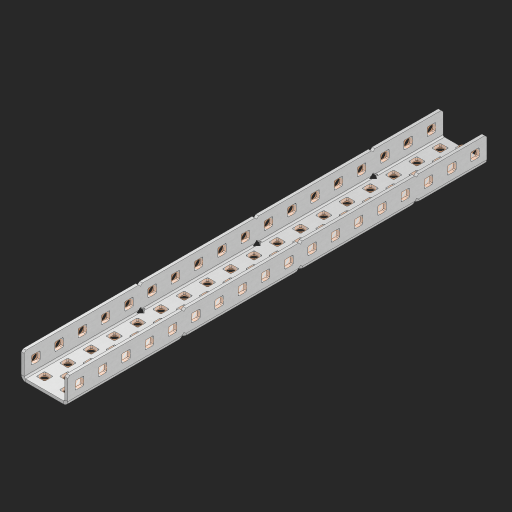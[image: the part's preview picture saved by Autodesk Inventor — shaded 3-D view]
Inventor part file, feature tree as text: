
AUTODESK INVENTOR PART (.ipt)
format: ipt  version: 2023 (Build 270158000, 158)  size: 1,305,088 bytes
history: native  units: in
note: dims shown in document units (in); Inventor stores cm internally (conversion verified against a paired STEP export)
features: other x97, extrude x88, sheet_metal_op x11, sketch x10, pattern_linear x2, mirror x1, chamfer x1
ambient origin geometry x8: Origin, YZ Plane, XZ Plane, XY Plane, X Axis, Y Axis, Z Axis, Center Point
bodies: Solid1 (feature_tree), Body (feature_tree)
feature tree (210):
  sheet_metal_op  "Flanges"
  other  "Flange Pattern Plane"
  other  "Flange Pattern Sketch"
  sheet_metal_op  "Flange Pattern"
  sheet_metal_op  "Body Pattern"
  pattern_linear  "Center Pattern"  Spacing1=0.0625in  [1 undecoded]
  other  "Arc Length"
  mirror  "Notch Mirror"
  pattern_linear  "Notch Pattern"  Spacing1=0.182in  [1 undecoded]
  chamfer  "End Chamfer"
  extrude  "Half Cut"  Depth=0.02in
  sketch  "Sketch1"  dims[d0=1.0in]
  other  "Plate1"
  sketch  "Sketch2"  dims[d1=9.0in]
  other  "Plate2"
  sheet_metal_op  "Bend1"
  sheet_metal_op  "Corner1"
  sketch  "Sketch3"  dims[d2=0.0625in]
  sketch  "Sketch7"  dims[d3=0.0625in]
  other  "Srf1"
  other  "Srf2"
  sketch  "Sketch8"  dims[d4=0.0312in]
  sketch  "Sketch9"  dims[d5=0.125in]
  other  "Srf91"
  sheet_metal_op  "Body Pattern Sketch"
  other  "Srf92"
  sketch  "Sketch13"  dims[d6=0.0625in]
  sketch  "Sketch14"  dims[d7=0.5in d8=90.0deg d9=0.0312in]
  sketch  "Sketch15"  dims[d10=0.25in]
  sketch  "Sketch16"  dims[d11=0.0625in d12=0.0625in d16=0.182in d17=0.02in d18=0.0625in d19=0.0in d20=0.25in d21=0.25in d38=7.0866in d40=0.5in d41=0.7874in d43=1.0in d46=0.172in d47=1.0in d48=0.0in d49=0.182in d50=0.02in d51=0.25in d52=0.25in d53=0.0625in d54=0.0in d55=0.172in d56=1.0in d57=0.0in d58=0.25in d60=7.0866in d62=0.5in d63=0.7874in d65=0.5in d85=0.1473in d86=0.1782in d88=0.04in d89=0.0625in d90=0.0in d91=0.04in d92=0.0491in d95=2.5in d96=0.04in d97=0.25in d98=45.0deg d99=0.25in d100=0.5in d101=0.0in d102=2.497in d106=0.182in d107=0.02in d108=0.5in d109=0.5in d110=0.0625in d111=0.0in d112=0.172in d113=0.5in d114=0.0in d117=0.5in d118=0.5in d119=0.5in]
  other  "Srf786"
  other  "Srf823"
  other  "Srf824"
  other  "Srf825"
  other  "Srf826"
  other  "Srf827"
  other  "Srf828"
  other  "Srf829"
  other  "Srf856"
  other  "Srf857"
  other  "Srf858"
  other  "Srf859"
  other  "Srf860"
  other  "Srf861"
  other  "Srf862"
  other  "Srf889"
  other  "Srf890"
  other  "Srf891"
  other  "Srf892"
  other  "Srf893"
  other  "Srf894"
  other  "Srf895"
  other  "Srf896"
  other  "Srf922"
  other  "Srf923"
  other  "Srf924"
  other  "Srf925"
  other  "Srf926"
  other  "Srf959"
  other  "Srf960"
  other  "Srf961"
  other  "Srf962"
  other  "Srf963"
  other  "Srf996"
  other  "Srf997"
  other  "Srf998"
  other  "Srf999"
  other  "Srf1000"
  other  "Srf1143"
  other  "Srf1144"
  other  "Srf1145"
  other  "Srf1146"
  other  "Srf1147"
  other  "Srf1148"
  other  "Srf1149"
  other  "Srf1150"
  other  "Srf1151"
  other  "Srf1152"
  other  "Srf1153"
  other  "Srf1154"
  other  "Srf1155"
  other  "Srf1156"
  other  "Srf1157"
  other  "Srf1158"
  other  "Srf1159"
  other  "Srf1160"
  other  "Srf1161"
  other  "Srf1162"
  other  "Srf1163"
  other  "Srf1164"
  other  "Srf1199"
  other  "Srf1200"
  other  "Srf1201"
  other  "Srf1202"
  other  "Srf1203"
  other  "Srf1204"
  other  "Srf1205"
  other  "Srf1206"
  other  "Srf1207"
  other  "Srf1208"
  other  "Srf1209"
  other  "Srf1210"
  other  "Srf1211"
  other  "Srf1212"
  other  "Srf1213"
  other  "Srf1214"
  other  "Srf1215"
  other  "Srf1216"
  other  "Srf1217"
  other  "Srf1218"
  other  "Srf1219"
  other  "Srf1220"
  other  "Srf1255"
  other  "Srf1256"
  other  "Srf1257"
  other  "Srf1258"
  sheet_metal_op  "Flange Stamp"
  sheet_metal_op  "Flange Circle"
  sheet_metal_op  "Body Stamp"
  sheet_metal_op  "Body Circle"
  other  "Center Stamp"
  other  "Center Circle"
  sheet_metal_op  "Notch"
  extrude  "ExtrusionSrf2"  Depth=0.0625in
  extrude  "ExtrusionSrf92"  TaperAngle=0.0deg  [1 undecoded]
  extrude  "ExtrusionSrf823"  Depth=0.5in
  extrude  "ExtrusionSrf824"  Depth=0.5in
  extrude  "ExtrusionSrf825"  Depth=0.5in
  extrude  "ExtrusionSrf826"  Depth=0.5in
  extrude  "ExtrusionSrf827"  Depth=1.0in TaperAngle=0.0deg
  extrude  "ExtrusionSrf828"  Depth=0.5in
  extrude  "ExtrusionSrf829"  Depth=0.02in
  extrude  "ExtrusionSrf856"  Depth=0.5in
  extrude  "ExtrusionSrf857"  Depth=0.5in
  extrude  "ExtrusionSrf858"  Depth=0.0625in
  extrude  "ExtrusionSrf859"  TaperAngle=0.0deg  [1 undecoded]
  extrude  "ExtrusionSrf860"  Depth=0.5in
  extrude  "ExtrusionSrf861"  Depth=1.0in TaperAngle=0.0deg
  extrude  "ExtrusionSrf862"  Depth=0.5in
  extrude  "ExtrusionSrf889"  Depth=0.5in
  extrude  "ExtrusionSrf890"  Depth=0.5in
  extrude  "ExtrusionSrf891"  Depth=0.5in
  extrude  "ExtrusionSrf892"  Depth=0.5in
  extrude  "ExtrusionSrf893"  Depth=0.5in
  extrude  "ExtrusionSrf894"  Depth=0.0625in
  extrude  "ExtrusionSrf895"  TaperAngle=0.0deg  [1 undecoded]
  extrude  "ExtrusionSrf896"  Depth=0.5in
  extrude  "ExtrusionSrf922"  Depth=0.5in
  extrude  "ExtrusionSrf923"  Depth=2.5in
  extrude  "ExtrusionSrf924"  Depth=0.5in TaperAngle=45.0deg
  extrude  "ExtrusionSrf925"  Depth=0.5in
  extrude  "ExtrusionSrf926"  Depth=0.5in TaperAngle=0.0deg
  extrude  "ExtrusionSrf959"  Depth=0.5in
  extrude  "ExtrusionSrf960"  Depth=0.5in
  extrude  "ExtrusionSrf961"  Depth=0.02in
  extrude  "ExtrusionSrf962"  Depth=0.5in
  extrude  "ExtrusionSrf963"  Depth=0.5in
  extrude  "ExtrusionSrf996"  Depth=0.0625in
  extrude  "ExtrusionSrf997"  TaperAngle=0.0deg  [1 undecoded]
  extrude  "ExtrusionSrf998"  Depth=0.5in
  extrude  "ExtrusionSrf999"  Depth=0.5in TaperAngle=0.0deg
  extrude  "ExtrusionSrf1000"  Depth=0.5in
  extrude  "ExtrusionSrf1143"  Depth=0.5in
  extrude  "ExtrusionSrf1144"  Depth=0.5in
  extrude  "ExtrusionSrf1145"  [1 undecoded]
  extrude  "ExtrusionSrf1146"  [1 undecoded]
  extrude  "ExtrusionSrf1147"  [1 undecoded]
  extrude  "ExtrusionSrf1148"  [1 undecoded]
  extrude  "ExtrusionSrf1149"  [1 undecoded]
  extrude  "ExtrusionSrf1150"  [1 undecoded]
  extrude  "ExtrusionSrf1151"  [1 undecoded]
  extrude  "ExtrusionSrf1152"  [1 undecoded]
  extrude  "ExtrusionSrf1153"  [1 undecoded]
  extrude  "ExtrusionSrf1154"  [1 undecoded]
  extrude  "ExtrusionSrf1155"  [1 undecoded]
  extrude  "ExtrusionSrf1156"  [1 undecoded]
  extrude  "ExtrusionSrf1157"  [1 undecoded]
  extrude  "ExtrusionSrf1158"  [1 undecoded]
  extrude  "ExtrusionSrf1159"  [1 undecoded]
  extrude  "ExtrusionSrf1160"  [1 undecoded]
  extrude  "ExtrusionSrf1161"  [1 undecoded]
  extrude  "ExtrusionSrf1162"  [1 undecoded]
  extrude  "ExtrusionSrf1163"  [1 undecoded]
  extrude  "ExtrusionSrf1164"  [1 undecoded]
  extrude  "ExtrusionSrf1199"  [1 undecoded]
  extrude  "ExtrusionSrf1200"  [1 undecoded]
  extrude  "ExtrusionSrf1201"  [1 undecoded]
  extrude  "ExtrusionSrf1202"  [1 undecoded]
  extrude  "ExtrusionSrf1203"  [1 undecoded]
  extrude  "ExtrusionSrf1204"  [1 undecoded]
  extrude  "ExtrusionSrf1205"  [1 undecoded]
  extrude  "ExtrusionSrf1206"  [1 undecoded]
  extrude  "ExtrusionSrf1207"  [1 undecoded]
  extrude  "ExtrusionSrf1208"  [1 undecoded]
  extrude  "ExtrusionSrf1209"  [1 undecoded]
  extrude  "ExtrusionSrf1210"  [1 undecoded]
  extrude  "ExtrusionSrf1211"  [1 undecoded]
  extrude  "ExtrusionSrf1212"  [1 undecoded]
  extrude  "ExtrusionSrf1213"  [1 undecoded]
  extrude  "ExtrusionSrf1214"  [1 undecoded]
  extrude  "ExtrusionSrf1215"  [1 undecoded]
  extrude  "ExtrusionSrf1216"  [1 undecoded]
  extrude  "ExtrusionSrf1217"  [1 undecoded]
  extrude  "ExtrusionSrf1218"  [1 undecoded]
  extrude  "ExtrusionSrf1219"  [1 undecoded]
  extrude  "ExtrusionSrf1220"  [1 undecoded]
  extrude  "ExtrusionSrf1255"  [1 undecoded]
  extrude  "ExtrusionSrf1256"  [1 undecoded]
  extrude  "ExtrusionSrf1257"  [1 undecoded]
  extrude  "ExtrusionSrf1258"  [1 undecoded]
note: 52 required parameter values undecoded (feature->parameter linkage not recoverable at this tier; creation-order binding heuristic only, values carry confidence <= 0.55)
